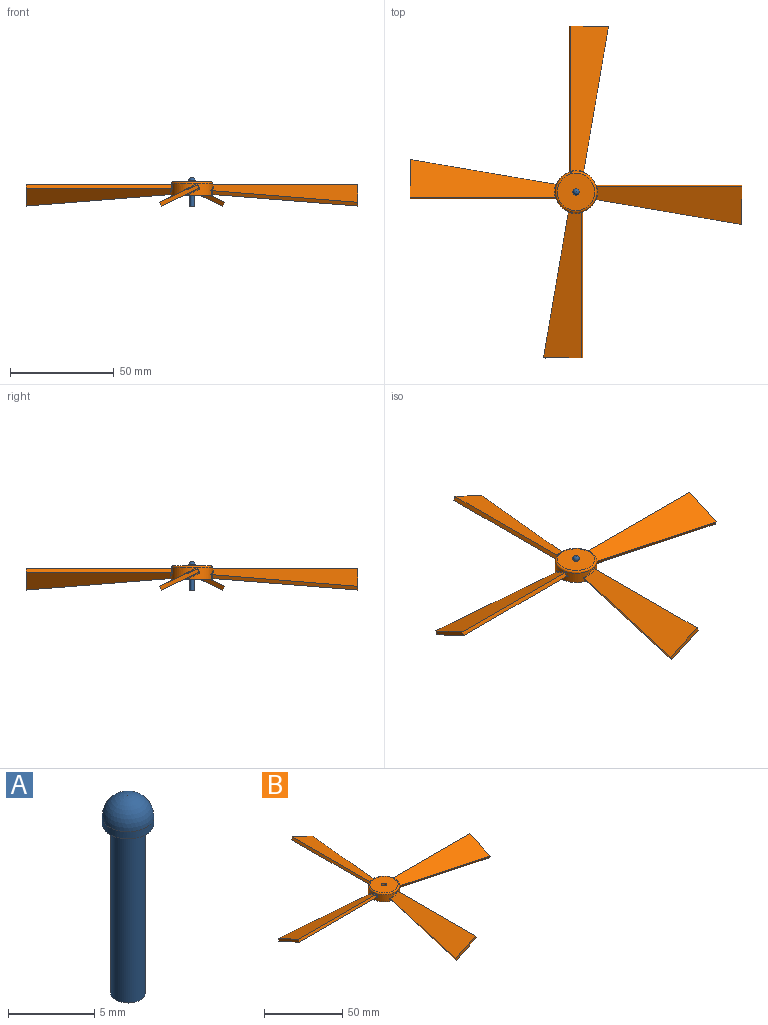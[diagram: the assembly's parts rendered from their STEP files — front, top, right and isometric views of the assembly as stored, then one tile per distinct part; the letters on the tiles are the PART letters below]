
ASSEMBLY  parts=2 mates=1
PART A: 5 faces, bbox 3x3x14 mm
  f0: cylinder r=1mm len=12mm, axis (0,0,-1), area 75.4mm2, adj f1,f3
  f1: plane 2x2mm, normal (0,0,-1), area 3.1mm2, adj f0
  f2: cylinder r=1.5mm len=3mm, axis (0,0,-1), area 4.7mm2, adj f3,f4
  f3: plane 3x3mm, normal (0,0,-1), area 3.9mm2, adj f0,f2
  f4: sphere r=1.5mm, area 14.1mm2, adj f2
PART B: 53 faces, bbox 160x160x11.8 mm
  f0: cylinder r=10mm len=12.28mm, axis (0,0,-1), area 63.5mm2, adj f4,f22,f23,f35,f37,f51
  f1: cylinder r=10mm len=12.28mm, axis (0,0,-1), area 63.5mm2, adj f4,f33,f34,f46,f48,f51
  f2: cylinder r=10mm len=12.28mm, axis (0,0,-1), area 63.5mm2, adj f4,f13,f15,f44,f45,f51
  f3: cylinder r=10mm len=12.28mm, axis (0,0,-1), area 63.5mm2, adj f4,f11,f12,f24,f26,f51
  f4: plane 20.05x20.05mm, normal (0,0,-1), area 307.1mm2, adj f0,f1,f2,f3,f14,f16,f25,f36
  f5: plane 70.21x1.85mm, normal (0,0.91,0.42), area 140.1mm2, adj f6,f8,f9,f11,f12,f13
  f6: plane 70.25x18.13mm, normal (0,-0.42,0.91), area 938.5mm2, adj f5,f7,f8,f13
  f7: plane 70.26x12.73mm, normal (-0.18,-0.89,-0.42), area 142.6mm2, adj f6,f8,f9,f13,f14,f15
  f8: plane 18.97x10.27mm, normal (1,0,0), area 40mm2, adj f5,f6,f7,f9
  f9: plane 70.12x18.13mm, normal (0,0.42,-0.91), area 938.3mm2, adj f5,f7,f8,f12,f14
  f10: plane 0.41x0.11mm, normal (0,0,1), area 0mm2, adj f11,f13,f51
  f11: bspline ~2.82x1.48mm, area 1.6mm2, adj f3,f5,f10,f12,f13
  f12: bspline ~6.34x3.4mm, area 5.1mm2, adj f3,f5,f9,f11,f14
  f13: bspline ~6.97x3.7mm, area 5.5mm2, adj f2,f5,f6,f7,f10,f11,f15
  f14: bspline ~1.33x0.79mm, area 0.4mm2, adj f4,f7,f9,f12,f15
  f15: bspline ~2.62x1.29mm, area 1.7mm2, adj f2,f7,f13,f14
  f16: cylinder r=1.5mm len=6.5mm, axis (0,0,-1), area 61.3mm2, adj f4,f49
  f17: plane 70.21x1.85mm, normal (-0.91,0,0.42), area 140.1mm2, adj f18,f20,f21,f22,f23,f24
  f18: plane 70.25x18.13mm, normal (0.42,0,0.91), area 938.5mm2, adj f17,f19,f20,f24
  f19: plane 70.26x12.73mm, normal (0.89,-0.18,-0.42), area 142.6mm2, adj f18,f20,f21,f24,f25,f26
  f20: plane 18.97x10.27mm, normal (0,1,0), area 40mm2, adj f17,f18,f19,f21
  f21: plane 70.12x18.13mm, normal (-0.42,0,-0.91), area 938.3mm2, adj f17,f19,f20,f23,f25
  f22: bspline ~2.82x1.48mm, area 1.6mm2, adj f0,f17,f23,f24,f52
  f23: bspline ~6.34x3.4mm, area 5.1mm2, adj f0,f17,f21,f22,f25
  f24: bspline ~6.97x3.7mm, area 5.5mm2, adj f3,f17,f18,f19,f22,f26,f50
  f25: bspline ~1.33x0.79mm, area 0.4mm2, adj f4,f19,f21,f23,f26
  f26: bspline ~2.62x1.29mm, area 1.7mm2, adj f3,f19,f24,f25
  f27: plane 70.21x1.85mm, normal (0,-0.91,0.42), area 140.1mm2, adj f28,f30,f31,f33,f34,f35
  f28: plane 70.25x18.13mm, normal (0,0.42,0.91), area 938.5mm2, adj f27,f29,f30,f35
  f29: plane 70.26x12.73mm, normal (0.18,0.89,-0.42), area 142.6mm2, adj f28,f30,f31,f35,f36,f37
  f30: plane 18.97x10.27mm, normal (-1,0,0), area 40mm2, adj f27,f28,f29,f31
  f31: plane 70.12x18.13mm, normal (0,-0.42,-0.91), area 938.3mm2, adj f27,f29,f30,f34,f36
  f32: plane 0.41x0.11mm, normal (0,0,1), area 0mm2, adj f33,f35,f51
  f33: bspline ~2.82x1.48mm, area 1.6mm2, adj f1,f27,f32,f34,f35
  f34: bspline ~6.34x3.4mm, area 5.1mm2, adj f1,f27,f31,f33,f36
  f35: bspline ~6.97x3.7mm, area 5.5mm2, adj f0,f27,f28,f29,f32,f33,f37
  f36: bspline ~1.33x0.79mm, area 0.4mm2, adj f4,f29,f31,f34,f37
  f37: bspline ~2.62x1.29mm, area 1.7mm2, adj f0,f29,f35,f36
  f38: plane 70.21x1.85mm, normal (0.91,0,0.42), area 140.1mm2, adj f39,f41,f42,f44,f45,f46
  f39: plane 70.25x18.13mm, normal (-0.42,0,0.91), area 938.5mm2, adj f38,f40,f41,f46
  f40: plane 70.26x12.73mm, normal (-0.89,0.18,-0.42), area 142.6mm2, adj f39,f41,f42,f46,f47,f48
  f41: plane 18.97x10.27mm, normal (0,-1,0), area 40mm2, adj f38,f39,f40,f42
  f42: plane 70.12x18.13mm, normal (0.42,0,-0.91), area 938.3mm2, adj f38,f40,f41,f45,f47
  f43: plane 0.41x0.11mm, normal (0,0,1), area 0mm2, adj f44,f46,f51
  f44: bspline ~2.82x1.48mm, area 1.6mm2, adj f2,f38,f43,f45,f46
  f45: bspline ~6.34x3.4mm, area 5.1mm2, adj f2,f38,f42,f44,f47
  f46: bspline ~6.97x3.7mm, area 5.5mm2, adj f1,f38,f39,f40,f43,f44,f48
  f47: bspline ~1.33x0.79mm, area 0.4mm2, adj f4,f40,f42,f45,f48
  f48: bspline ~2.62x1.29mm, area 1.7mm2, adj f1,f40,f46,f47
  f49: plane 18x18mm, normal (0,0,1), area 247.4mm2, adj f16,f50,f51,f52
  f50: bspline ~1.08x1mm, area 0.4mm2, adj f24,f49,f51,f52
  f51: torus R=9mm, axis (0,0,1), area 94.5mm2, adj f0,f1,f2,f3,f10,f32,f43,f49
  f52: bspline ~1.05x1mm, area 0.2mm2, adj f22,f49,f50,f51
PLACE A t=(0,0,-4)mm fixed
PLACE B t=(0,0,4.5)mm
MATE revolute B.f16 <-> A.f0  axis (0,0,1) through (0,0,8)mm
